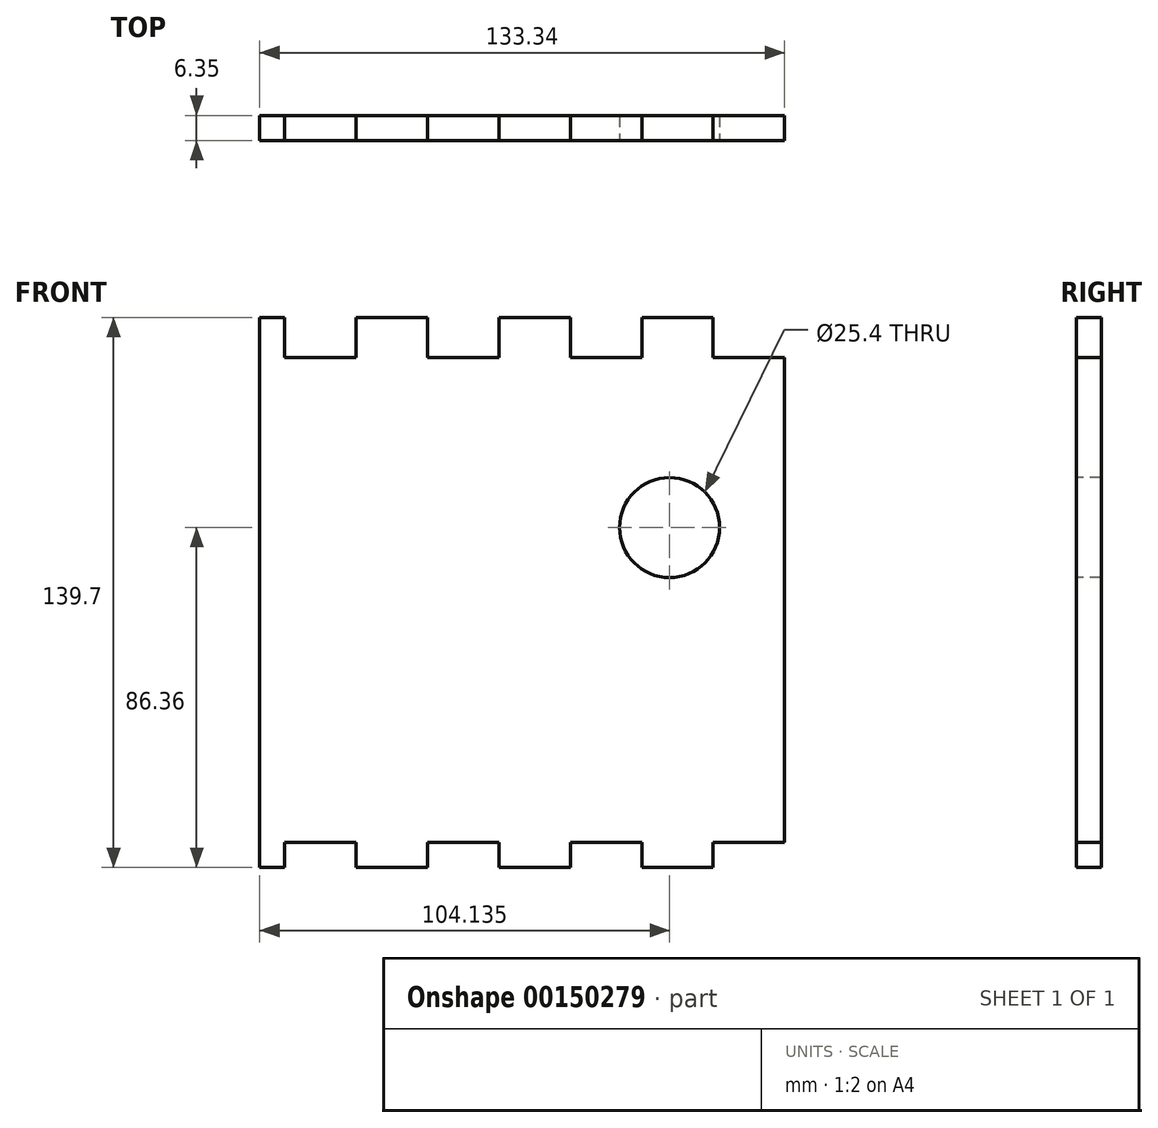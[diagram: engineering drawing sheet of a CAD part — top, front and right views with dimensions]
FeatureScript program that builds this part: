
annotation { "Feature Type Name" : "Feature", "Feature Type Description" : "" }
export const myFeature = defineFeature(function(context is Context, id is Id, definition is map)
    precondition{}
    {
        {
            var Q0;
            Q0=qCreatedBy(makeId("Front.planeOp"),FACE);
            var sketch = newSketch(context, id + "F0", { "sketchPlane" : qUnion([Q0])});
            skLineSegment(sketch, "E0.bottom", {"start": v(-66.68, 69.85) * mm, "end": v(66.67, 69.85) * mm});
            skLineSegment(sketch, "E0.top", {"start": v(-66.68, -69.85) * mm, "end": v(66.67, -69.85) * mm});
            skLineSegment(sketch, "E0.left", {"start": v(-66.68, 69.85) * mm, "end": v(-66.68, -69.85) * mm});
            skLineSegment(sketch, "E0.right", {"start": v(66.67, 69.85) * mm, "end": v(66.67, -69.85) * mm});
            skSolve(sketch);
        }
        {
            var Q0;
            Q0 = qSketchRegion(id + "F0", true);
            extrude(context, id + "F1", {"entities" : qUnion([Q0]), "depth" : 6.35 * mm});
        }
        {
            var Q0;
            Q0=makeQuery(id+"F1.opExtrude","CAP_FACE",FACE,{"disambiguationData":[OSD([sQuery(id+"F0.wireOp",EDGE,"E0.bottom"),sQuery(id+"F0.wireOp",EDGE,"E0.top"),sQuery(id+"F0.wireOp",EDGE,"E0.left"),sQuery(id+"F0.wireOp",EDGE,"E0.right")])],"isStart":false});
            var sketch = newSketch(context, id + "F2", { "sketchPlane" : qUnion([Q0])});
            skLineSegment(sketch, "E1.bottom", {"start": v(-66.68, 69.85) * mm, "end": v(66.67, 69.85) * mm});
            skLineSegment(sketch, "E1.top", {"start": v(-66.68, 59.69) * mm, "end": v(66.67, 59.69) * mm});
            skLineSegment(sketch, "E1.left", {"start": v(-66.68, 69.85) * mm, "end": v(-66.68, 59.69) * mm});
            skLineSegment(sketch, "E1.right", {"start": v(66.67, 69.85) * mm, "end": v(66.67, 59.69) * mm});
            skLineSegment(sketch, "E2", {"start": v(-60.33, 69.85) * mm, "end": v(-60.33, 59.69) * mm});
            skLineSegment(sketch, "E3", {"start": v(-42.18, 69.85) * mm, "end": v(-42.18, 59.69) * mm});
            skLineSegment(sketch, "E4", {"start": v(-24.04, 69.85) * mm, "end": v(-24.04, 59.69) * mm});
            skLineSegment(sketch, "E5", {"start": v(-5.9, 69.85) * mm, "end": v(-5.9, 59.7) * mm});
            skLineSegment(sketch, "E6", {"start": v(12.25, 69.85) * mm, "end": v(12.25, 59.7) * mm});
            skLineSegment(sketch, "E7", {"start": v(30.39, 69.85) * mm, "end": v(30.39, 59.7) * mm});
            skLineSegment(sketch, "E8", {"start": v(48.53, 69.85) * mm, "end": v(48.53, 59.7) * mm});
            skLineSegment(sketch, "E9.bottom", {"start": v(-66.68, -63.5) * mm, "end": v(66.67, -63.5) * mm});
            skLineSegment(sketch, "E9.top", {"start": v(-66.68, -69.85) * mm, "end": v(66.67, -69.85) * mm});
            skLineSegment(sketch, "E9.left", {"start": v(-66.68, -63.5) * mm, "end": v(-66.68, -69.85) * mm});
            skLineSegment(sketch, "E9.right", {"start": v(66.67, -63.5) * mm, "end": v(66.67, -69.85) * mm});
            skLineSegment(sketch, "E10", {"start": v(-60.33, 59.69) * mm, "end": v(-60.33, -69.85) * mm});
            skLineSegment(sketch, "E11", {"start": v(-42.18, 59.69) * mm, "end": v(-42.18, -69.85) * mm});
            skLineSegment(sketch, "E12", {"start": v(-24.04, 59.69) * mm, "end": v(-24.04, -69.85) * mm});
            skLineSegment(sketch, "E13", {"start": v(-5.9, 59.7) * mm, "end": v(-5.9, -69.85) * mm});
            skLineSegment(sketch, "E14", {"start": v(12.25, 59.7) * mm, "end": v(12.25, -69.85) * mm});
            skLineSegment(sketch, "E15", {"start": v(30.39, 59.7) * mm, "end": v(30.39, -69.85) * mm});
            skLineSegment(sketch, "E16", {"start": v(48.53, 59.7) * mm, "end": v(48.53, -69.85) * mm});
            skSolve(sketch);
        }
        {
            var Q0;
            {var subQ0=sQuery(id+"F2.wireOp",EDGE,"E1.right");Q0=makeQuery(id+"F2.imprint","IMPRINT",FACE,{"disambiguationData":[TD([[makeQuery(id+"F2.imprint","IMPRINT",EDGE,{"derivedFrom":subQ0}),-1.0]])]});}
            var Q1;
            {var subQ0=sQuery(id+"F2.wireOp",EDGE,"E2");Q1=makeQuery(id+"F2.imprint","IMPRINT",FACE,{"disambiguationData":[TD([[makeQuery(id+"F2.imprint","IMPRINT",EDGE,{"derivedFrom":subQ0}),1.0]])]});}
            var Q2;
            {var subQ0=sQuery(id+"F2.wireOp",EDGE,"E4");Q2=makeQuery(id+"F2.imprint","IMPRINT",FACE,{"disambiguationData":[TD([[makeQuery(id+"F2.imprint","IMPRINT",EDGE,{"derivedFrom":subQ0}),1.0]])]});}
            var Q3;
            {var subQ0=sQuery(id+"F2.wireOp",EDGE,"E6");Q3=makeQuery(id+"F2.imprint","IMPRINT",FACE,{"disambiguationData":[TD([[makeQuery(id+"F2.imprint","IMPRINT",EDGE,{"derivedFrom":subQ0}),1.0]])]});}
            var Q4;
            {var subQ0=sQuery(id+"F2.wireOp",EDGE,"E10");var subQ1=sQuery(id+"F2.wireOp",EDGE,"E9.bottom");var subQ2=makeQuery(id+"F2.imprint","INTERSECT",VERTEX,{"derivedFrom":[subQ1,subQ0]});Q4=makeQuery(id+"F2.imprint","IMPRINT",FACE,{"disambiguationData":[TD([[makeQuery(id+"F2.imprint","IMPRINT",EDGE,{"disambiguationData":[TD([[subQ2,-1.0]])],"derivedFrom":subQ1}),-1.0]])]});}
            var Q5;
            {var subQ0=sQuery(id+"F2.wireOp",EDGE,"E12");var subQ1=sQuery(id+"F2.wireOp",EDGE,"E9.bottom");var subQ2=makeQuery(id+"F2.imprint","INTERSECT",VERTEX,{"derivedFrom":[subQ1,subQ0]});Q5=makeQuery(id+"F2.imprint","IMPRINT",FACE,{"disambiguationData":[TD([[makeQuery(id+"F2.imprint","IMPRINT",EDGE,{"disambiguationData":[TD([[subQ2,-1.0]])],"derivedFrom":subQ1}),-1.0]])]});}
            var Q6;
            {var subQ0=sQuery(id+"F2.wireOp",EDGE,"E14");var subQ1=sQuery(id+"F2.wireOp",EDGE,"E9.bottom");var subQ2=makeQuery(id+"F2.imprint","INTERSECT",VERTEX,{"derivedFrom":[subQ1,subQ0]});Q6=makeQuery(id+"F2.imprint","IMPRINT",FACE,{"disambiguationData":[TD([[makeQuery(id+"F2.imprint","IMPRINT",EDGE,{"disambiguationData":[TD([[subQ2,-1.0]])],"derivedFrom":subQ1}),-1.0]])]});}
            var Q7;
            {var subQ0=sQuery(id+"F2.wireOp",EDGE,"E9.right");Q7=makeQuery(id+"F2.imprint","IMPRINT",FACE,{"disambiguationData":[TD([[makeQuery(id+"F2.imprint","IMPRINT",EDGE,{"derivedFrom":subQ0}),-1.0]])]});}
            extrude(context, id + "F3", {"entities" : qUnion([Q0, Q1, Q2, Q3, Q4, Q5, Q6, Q7]), "operationType" : NewBodyOperationType.REMOVE, "oppositeDirection" : true, "depth" : 25.4 * mm});
        }
        {
            var Q0;
            Q0=makeQuery(id+"F1.opExtrude","CAP_FACE",FACE,{"disambiguationData":[OSD([sQuery(id+"F0.wireOp",EDGE,"E0.bottom"),sQuery(id+"F0.wireOp",EDGE,"E0.top"),sQuery(id+"F0.wireOp",EDGE,"E0.left"),sQuery(id+"F0.wireOp",EDGE,"E0.right")])],"isStart":false});
            var sketch = newSketch(context, id + "F4", { "sketchPlane" : qUnion([Q0])});
            skCircle(sketch, "E17", {"center": v(37.46, 16.5) * mm, "radius": 12.7 * mm});
            skSolve(sketch);
        }
        {
            var Q0;
            Q0=makeQuery(id+"F4.imprint","IMPRINT",FACE,{"disambiguationData":[TD([[makeQuery(id+"F4.imprint","IMPRINT",EDGE,{"derivedFrom":sQuery(id+"F4.wireOp",EDGE,"E17")}),1.0]])]});
            extrude(context, id + "F5", {"entities" : qUnion([Q0]), "operationType" : NewBodyOperationType.REMOVE, "oppositeDirection" : true, "depth" : 25.4 * mm});
        }
    });
